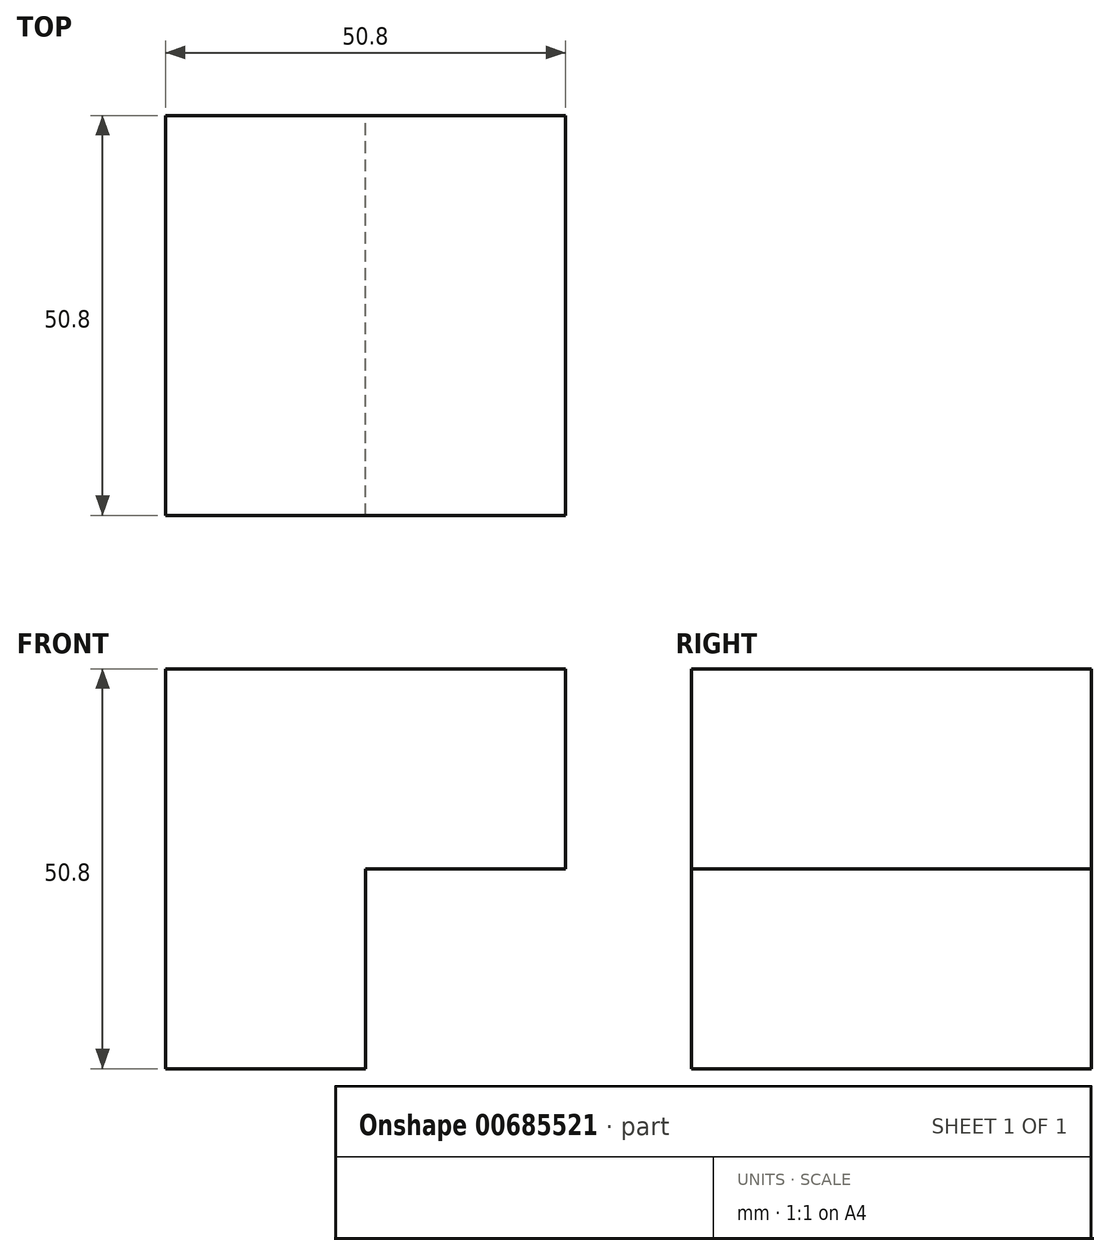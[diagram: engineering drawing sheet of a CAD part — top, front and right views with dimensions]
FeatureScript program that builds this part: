
annotation { "Feature Type Name" : "Feature", "Feature Type Description" : "" }
export const myFeature = defineFeature(function(context is Context, id is Id, definition is map)
    precondition{}
    {
        {
            var Q0;
            Q0=qCreatedBy(makeId("Front.planeOp"),FACE);
            var sketch = newSketch(context, id + "F0", { "sketchPlane" : qUnion([Q0])});
            skLineSegment(sketch, "E0", {"start": v(0, 0) * mm, "end": v(0, 50.8) * mm});
            skLineSegment(sketch, "E1", {"start": v(0, 50.8) * mm, "end": v(50.8, 50.8) * mm});
            skLineSegment(sketch, "E2", {"start": v(50.8, 50.8) * mm, "end": v(50.8, 25.4) * mm});
            skLineSegment(sketch, "E3", {"start": v(50.8, 25.4) * mm, "end": v(25.4, 25.4) * mm});
            skLineSegment(sketch, "E4", {"start": v(25.4, 25.4) * mm, "end": v(25.4, 0) * mm});
            skLineSegment(sketch, "E5", {"start": v(25.4, 0) * mm, "end": v(0, 0) * mm});
            skSolve(sketch);
        }
        {
            var Q0;
            Q0 = qSketchRegion(id + "F0", true);
            extrude(context, id + "F1", {"entities" : qUnion([Q0]), "depth" : 50.8 * mm, "offsetDistance" : 25.4 * mm});
        }
    });
